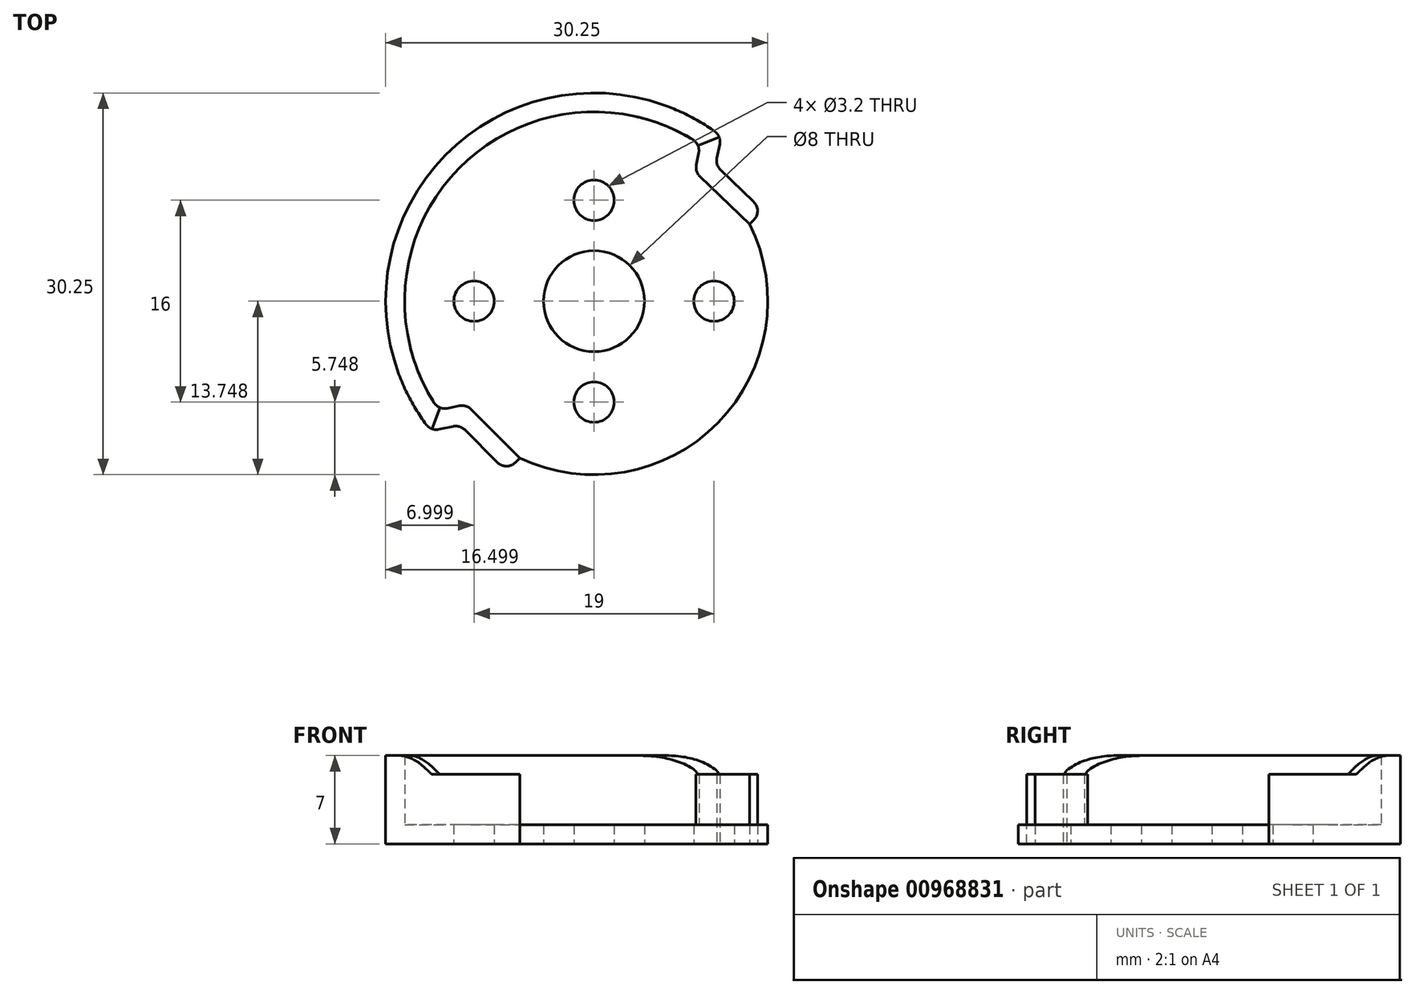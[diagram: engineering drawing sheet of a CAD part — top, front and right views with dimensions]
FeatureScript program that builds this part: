
annotation { "Feature Type Name" : "Feature", "Feature Type Description" : "" }
export const myFeature = defineFeature(function(context is Context, id is Id, definition is map)
    precondition{}
    {
        {
            var Q0;
            Q0=qCreatedBy(makeId("Top.planeOp"),FACE);
            var sketch = newSketch(context, id + "F0", { "sketchPlane" : qUnion([Q0])});
            skLineSegment(sketch, "E0.bottom", {"start": v(-22, 39) * mm, "end": v(22, 39) * mm});
            skLineSegment(sketch, "E0.top", {"start": v(-22, -39) * mm, "end": v(22, -39) * mm});
            skLineSegment(sketch, "E0.left", {"start": v(-22, 39) * mm, "end": v(-22, -39) * mm});
            skLineSegment(sketch, "E0.right", {"start": v(22, 39) * mm, "end": v(22, -39) * mm});
            skPoint(sketch, "E0.middle", {"position": v(0, 0) * mm});
            skArc(sketch, "E1", {"start": v(-65.64, 87.15) * mm, "mid": v(-84.75, 85.26) * mm, "end": v(-86.34, 66.12) * mm});
            skLineSegment(sketch, "E2", {"start": v(-84.18, 66.56) * mm, "end": v(-86.34, 66.12) * mm});
            skLineSegment(sketch, "E3", {"start": v(-66.07, 85) * mm, "end": v(-65.64, 87.15) * mm});
            skLineSegment(sketch, "E4", {"start": v(-84.18, 66.56) * mm, "end": v(-79.95, 62.3) * mm});
            skLineSegment(sketch, "E5", {"start": v(-66.07, 85) * mm, "end": v(-61.74, 80.84) * mm});
            skArc(sketch, "E6", {"start": v(-79.95, 62.3) * mm, "mid": v(-64.25, 65.1) * mm, "end": v(-61.74, 80.84) * mm});
            skLineSegment(sketch, "E7", {"start": v(-74.06, 74.74) * mm, "end": v(-83.56, 74.74) * mm});
            skLineSegment(sketch, "E8", {"start": v(-74.06, 74.74) * mm, "end": v(-64.56, 74.74) * mm});
            skLineSegment(sketch, "E9", {"start": v(-74.06, 74.74) * mm, "end": v(-74.06, 82.74) * mm});
            skLineSegment(sketch, "E10", {"start": v(-74.06, 74.74) * mm, "end": v(-74.06, 66.74) * mm});
            skLineSegment(sketch, "E11.0", {"start": v(-84.67, 64.93) * mm, "end": v(-81, 61.25) * mm});
            skLineSegment(sketch, "E11.1", {"start": v(-64.44, 85.5) * mm, "end": v(-60.7, 81.92) * mm});
            skLineSegment(sketch, "E11.2", {"start": v(-64.44, 85.5) * mm, "end": v(-63.99, 87.8) * mm});
            skArc(sketch, "E11.3", {"start": v(-63.99, 87.8) * mm, "mid": v(-85.82, 86.31) * mm, "end": v(-86.97, 64.46) * mm});
            skLineSegment(sketch, "E11.4", {"start": v(-84.67, 64.93) * mm, "end": v(-86.97, 64.46) * mm});
            skLineSegment(sketch, "E12", {"start": v(-79.95, 62.3) * mm, "end": v(-81, 61.25) * mm});
            skLineSegment(sketch, "E13", {"start": v(-60.7, 81.92) * mm, "end": v(-61.74, 80.84) * mm});
            skLineSegment(sketch, "E14", {"start": v(-63.99, 87.8) * mm, "end": v(-65.64, 87.15) * mm});
            skLineSegment(sketch, "E15", {"start": v(-86.34, 66.12) * mm, "end": v(-86.97, 64.46) * mm});
            skSolve(sketch);
        }
        {
            var Q0;
            Q0=makeQuery(id+"F0.imprint","IMPRINT",FACE,{"disambiguationData":[TD([[makeQuery(id+"F0.imprint","IMPRINT",EDGE,{"derivedFrom":sQuery(id+"F0.wireOp",EDGE,"E1")}),1.0]])]});
            extrude(context, id + "F1", {"entities" : qUnion([Q0]), "depth" : 1.5 * mm, "offsetDistance" : 25 * mm});
        }
        {
            var Q0;
            Q0=makeQuery(id+"F0.imprint","IMPRINT",FACE,{"disambiguationData":[TD([[makeQuery(id+"F0.imprint","IMPRINT",EDGE,{"derivedFrom":sQuery(id+"F0.wireOp",EDGE,"E2")}),1.0]])]});
            var Q1;
            Q1=makeQuery(id+"F0.imprint","IMPRINT",FACE,{"disambiguationData":[TD([[makeQuery(id+"F0.imprint","IMPRINT",EDGE,{"derivedFrom":sQuery(id+"F0.wireOp",EDGE,"E3")}),-1.0]])]});
            extrude(context, id + "F2", {"entities" : qUnion([Q0, Q1]), "operationType" : NewBodyOperationType.ADD, "depth" : 5.5 * mm, "offsetDistance" : 25 * mm});
        }
        {
            var Q0;
            Q0=makeQuery(id+"F0.imprint","IMPRINT",FACE,{"disambiguationData":[TD([[makeQuery(id+"F0.imprint","IMPRINT",EDGE,{"derivedFrom":sQuery(id+"F0.wireOp",EDGE,"E1")}),-1.0]])]});
            extrude(context, id + "F3", {"entities" : qUnion([Q0]), "operationType" : NewBodyOperationType.ADD, "depth" : 7 * mm, "offsetDistance" : 25 * mm});
        }
        {
            var Q0;
            Q0=makeQuery(id+"F3.opExtrude","CAP_EDGE",EDGE,{"disambiguationData":[OSD([sQuery(id+"F0.wireOp",EDGE,"E15")])],"isStart":false});
            var Q1;
            Q1=makeQuery(id+"F3.opExtrude","CAP_EDGE",EDGE,{"disambiguationData":[OSD([sQuery(id+"F0.wireOp",EDGE,"E14")])],"isStart":false});
            fillet(context, id + "F4", {"entities" : qUnion([Q0, Q1]), "radius" : 6 * mm, "tangentPropagation" : true, "allowEdgeOverflow" : false});
        }
        {
            var Q0;
            {var subQ0=sQuery(id+"F0.wireOp",EDGE,"E15");var subQ1=sQuery(id+"F0.wireOp",EDGE,"E11.4");var subQ2=sQuery(id+"F0.wireOp",EDGE,"E11.3");Q0=makeQuery(id+"F3.boolean.opBoolean","MERGE",EDGE,{"derivedFrom":[makeQuery(id+"F2.opExtrude","SWEPT_EDGE",EDGE,{"disambiguationData":[OSD([subQ2,subQ1,subQ0])]}),makeQuery(id+"F3.opExtrude","SWEPT_EDGE",EDGE,{"disambiguationData":[OSD([subQ2,subQ1,subQ0])]})]});}
            var Q1;
            Q1=makeQuery(id+"F2.opExtrude","SWEPT_EDGE",EDGE,{"disambiguationData":[OSD([sQuery(id+"F0.wireOp",EDGE,"E11.0"),sQuery(id+"F0.wireOp",EDGE,"E11.4")])]});
            var Q2;
            Q2=makeQuery(id+"F2.opExtrude","SWEPT_EDGE",EDGE,{"disambiguationData":[OSD([sQuery(id+"F0.wireOp",EDGE,"E11.0"),sQuery(id+"F0.wireOp",EDGE,"E12")])]});
            var Q3;
            Q3=makeQuery(id+"F2.opExtrude","SWEPT_EDGE",EDGE,{"disambiguationData":[OSD([sQuery(id+"F0.wireOp",EDGE,"E11.1"),sQuery(id+"F0.wireOp",EDGE,"E13")])]});
            var Q4;
            Q4=makeQuery(id+"F2.opExtrude","SWEPT_EDGE",EDGE,{"disambiguationData":[OSD([sQuery(id+"F0.wireOp",EDGE,"E11.1"),sQuery(id+"F0.wireOp",EDGE,"E11.2")])]});
            var Q5;
            {var subQ0=sQuery(id+"F0.wireOp",EDGE,"E14");var subQ1=sQuery(id+"F0.wireOp",EDGE,"E11.3");var subQ2=sQuery(id+"F0.wireOp",EDGE,"E11.2");Q5=makeQuery(id+"F3.boolean.opBoolean","MERGE",EDGE,{"derivedFrom":[makeQuery(id+"F2.opExtrude","SWEPT_EDGE",EDGE,{"disambiguationData":[OSD([subQ2,subQ1,subQ0])]}),makeQuery(id+"F3.opExtrude","SWEPT_EDGE",EDGE,{"disambiguationData":[OSD([subQ2,subQ1,subQ0])]})]});}
            var Q6;
            Q6=makeQuery(id+"F2.opExtrude","CAP_EDGE",EDGE,{"disambiguationData":[OSD([sQuery(id+"F0.wireOp",EDGE,"E14")])],"isStart":false});
            var Q7;
            Q7=makeQuery(id+"F2.opExtrude","CAP_EDGE",EDGE,{"disambiguationData":[OSD([sQuery(id+"F0.wireOp",EDGE,"E15")])],"isStart":false});
            var Q8;
            Q8=makeQuery(id+"F2.opExtrude","SWEPT_EDGE",EDGE,{"disambiguationData":[OSD([sQuery(id+"F0.wireOp",EDGE,"E2"),sQuery(id+"F0.wireOp",EDGE,"E4")])]});
            var Q9;
            Q9=makeQuery(id+"F2.opExtrude","SWEPT_EDGE",EDGE,{"disambiguationData":[OSD([sQuery(id+"F0.wireOp",EDGE,"E3"),sQuery(id+"F0.wireOp",EDGE,"E5")])]});
            var Q10;
            {var subQ0=sQuery(id+"F0.wireOp",EDGE,"E14");var subQ1=sQuery(id+"F0.wireOp",EDGE,"E3");var subQ2=sQuery(id+"F0.wireOp",EDGE,"E1");Q10=makeQuery(id+"F3.boolean.opBoolean","MERGE",EDGE,{"derivedFrom":[makeQuery(id+"F2.boolean.opBoolean","SPLIT",EDGE,{"derivedFrom":makeQuery(id+"F2.opExtrude","SWEPT_EDGE",EDGE,{"disambiguationData":[OSD([subQ2,subQ1,subQ0])]})}),makeQuery(id+"F3.opExtrude","SWEPT_EDGE",EDGE,{"disambiguationData":[OSD([subQ2,subQ1,subQ0])]})]});}
            var Q11;
            {var subQ0=sQuery(id+"F0.wireOp",EDGE,"E15");var subQ1=sQuery(id+"F0.wireOp",EDGE,"E2");var subQ2=sQuery(id+"F0.wireOp",EDGE,"E1");Q11=makeQuery(id+"F3.boolean.opBoolean","MERGE",EDGE,{"derivedFrom":[makeQuery(id+"F2.boolean.opBoolean","SPLIT",EDGE,{"derivedFrom":makeQuery(id+"F2.opExtrude","SWEPT_EDGE",EDGE,{"disambiguationData":[OSD([subQ2,subQ1,subQ0])]})}),makeQuery(id+"F3.opExtrude","SWEPT_EDGE",EDGE,{"disambiguationData":[OSD([subQ2,subQ1,subQ0])]})]});}
            fillet(context, id + "F5", {"entities" : qUnion([Q0, Q1, Q2, Q3, Q4, Q5, Q6, Q7, Q8, Q9, Q10, Q11]), "radius" : 1 * mm, "tangentPropagation" : true, "allowEdgeOverflow" : false});
        }
        {
            var Q0;
            Q0=sQuery(id+"F0.wireOp",VERTEX,"E7.end");
            var Q1;
            Q1=sQuery(id+"F0.wireOp",VERTEX,"E9.end");
            var Q2;
            Q2=sQuery(id+"F0.wireOp",VERTEX,"E8.end");
            var Q3;
            Q3=sQuery(id+"F0.wireOp",VERTEX,"E10.end");
            var Q4;
            Q4=makeQuery(id+"F1.opExtrude","SWEPT_BODY",BODY,{"disambiguationData":[OSD([sQuery(id+"F0.wireOp",EDGE,"E1"),sQuery(id+"F0.wireOp",EDGE,"E2"),sQuery(id+"F0.wireOp",EDGE,"E3"),sQuery(id+"F0.wireOp",EDGE,"E4"),sQuery(id+"F0.wireOp",EDGE,"E5"),sQuery(id+"F0.wireOp",EDGE,"E6")])]});
            hole(context, id + "F6", {"style" : HoleStyle.SIMPLE, "endStyle" : HoleEndStyle.BLIND, "oppositeDirection" : true, "holeDiameter" : 3.2 * mm, "holeDepth" : 4 * mm, "isTappedThrough" : true, "tappedDepth" : 12 * mm, "tapClearance" : 3, "locations" : qUnion([Q0, Q1, Q2, Q3]), "scope" : qUnion([Q4]), "majorDiameter" : 5 * mm});
        }
        {
            var Q0;
            Q0=sQuery(id+"F0.wireOp",VERTEX,"E11.3.center");
            var Q1;
            Q1=makeQuery(id+"F1.opExtrude","SWEPT_BODY",BODY,{"disambiguationData":[OSD([sQuery(id+"F0.wireOp",EDGE,"E1"),sQuery(id+"F0.wireOp",EDGE,"E2"),sQuery(id+"F0.wireOp",EDGE,"E3"),sQuery(id+"F0.wireOp",EDGE,"E4"),sQuery(id+"F0.wireOp",EDGE,"E5"),sQuery(id+"F0.wireOp",EDGE,"E6")])]});
            hole(context, id + "F7", {"style" : HoleStyle.SIMPLE, "endStyle" : HoleEndStyle.BLIND, "oppositeDirection" : true, "holeDiameter" : 8 * mm, "holeDepth" : 4 * mm, "isTappedThrough" : true, "tappedDepth" : 12 * mm, "tapClearance" : 3, "locations" : qUnion([Q0]), "scope" : qUnion([Q1])});
        }
    });
